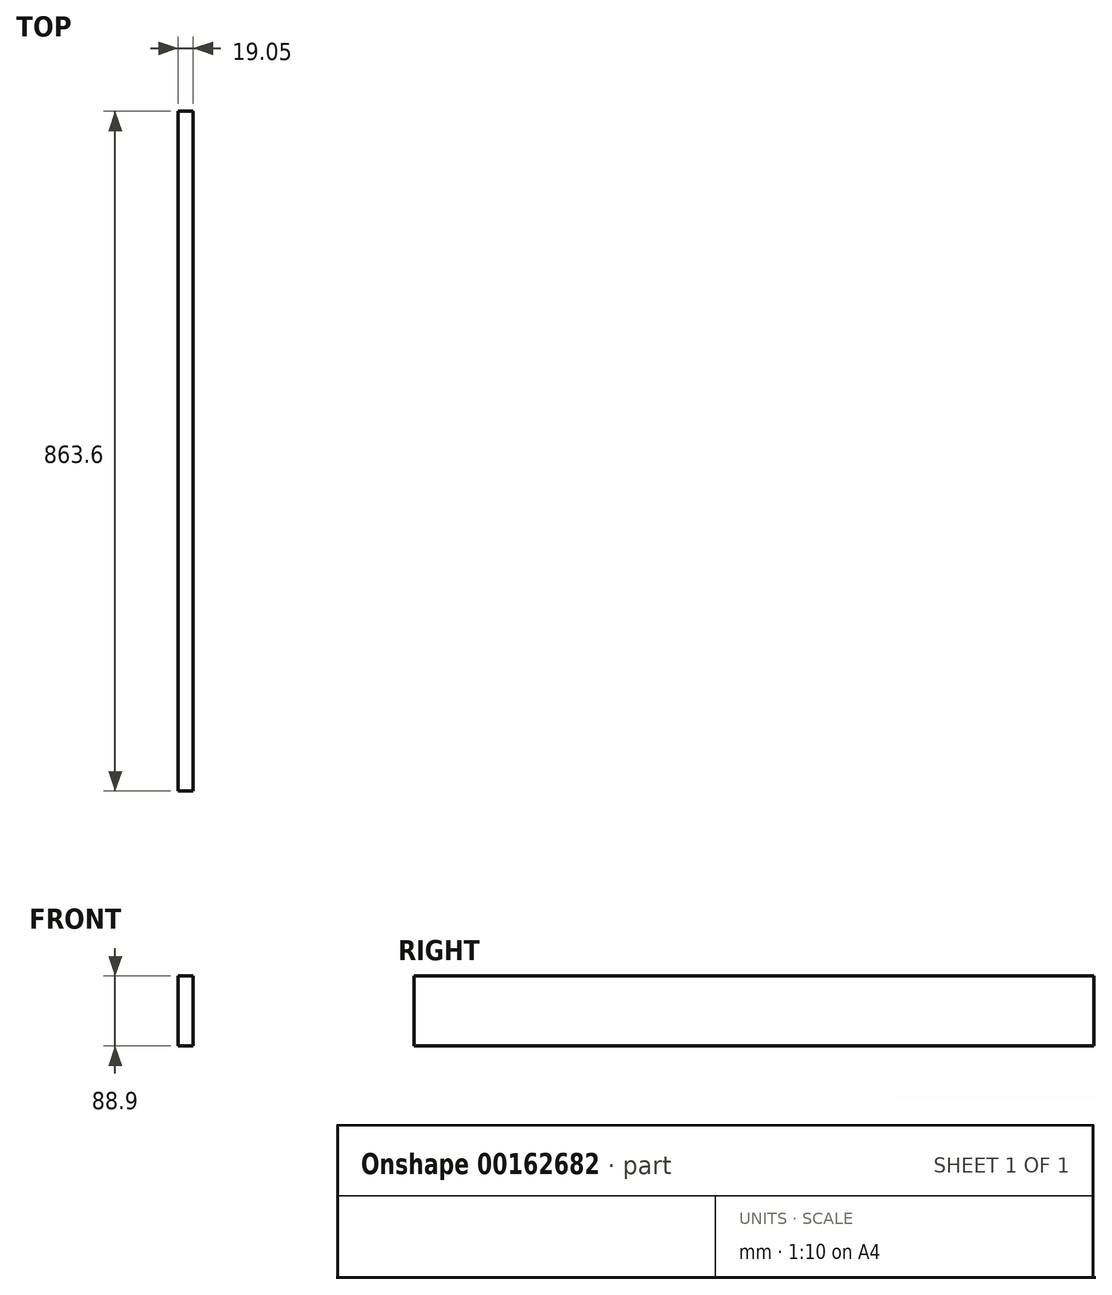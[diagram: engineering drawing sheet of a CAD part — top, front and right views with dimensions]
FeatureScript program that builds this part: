
annotation { "Feature Type Name" : "Feature", "Feature Type Description" : "" }
export const myFeature = defineFeature(function(context is Context, id is Id, definition is map)
    precondition{}
    {
        {
            var Q0;
            Q0=qCreatedBy(makeId("Right.planeOp"),FACE);
            var sketch = newSketch(context, id + "F0", { "sketchPlane" : qUnion([Q0])});
            skLineSegment(sketch, "E0.bottom", {"start": v(-436.4, 15.6) * mm, "end": v(427.2, 15.6) * mm});
            skLineSegment(sketch, "E0.top", {"start": v(-436.4, -73.3) * mm, "end": v(427.2, -73.3) * mm});
            skLineSegment(sketch, "E0.left", {"start": v(-436.4, 15.6) * mm, "end": v(-436.4, -73.3) * mm});
            skLineSegment(sketch, "E0.right", {"start": v(427.2, 15.6) * mm, "end": v(427.2, -73.3) * mm});
            skSolve(sketch);
        }
        {
            var Q0;
            Q0 = qSketchRegion(id + "F0", true);
            extrude(context, id + "F1", {"entities" : qUnion([Q0]), "depth" : 19.05 * mm});
        }
    });
